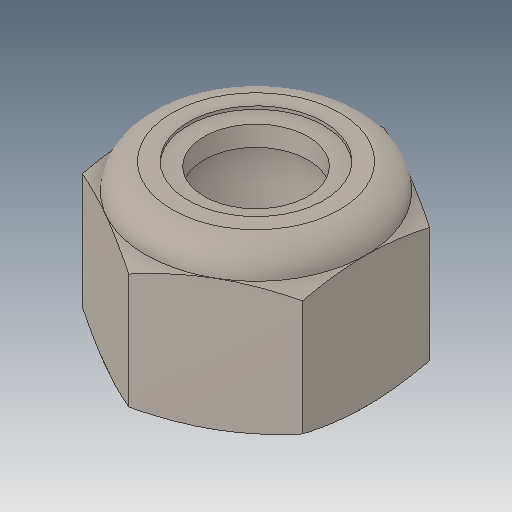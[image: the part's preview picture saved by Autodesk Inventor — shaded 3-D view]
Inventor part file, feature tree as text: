
AUTODESK INVENTOR PART (.ipt)
format: ipt  version: 2023.5 (Build 275446000, 446)  size: 176,640 bytes
history: native  units: in
note: dims shown in document units (in); Inventor stores cm internally (conversion verified against a paired STEP export)
features: other x1, revolve x1
ambient origin geometry x8: Origin, YZ Plane, XZ Plane, XY Plane, X Axis, Y Axis, Z Axis, Center Point
bodies: Solid1 (feature_tree), Solid2 (feature_tree)
feature tree (2):
  other  "Cut-Revolve2"
  revolve  "Revolve1"  [1 undecoded]
note: 1 required parameter value undecoded (feature->parameter linkage not recoverable at this tier; creation-order binding heuristic only, values carry confidence <= 0.55)
